# Revit family: JoistGirder_NewMillennium
name_source: partatom
category: Structural Framing
units: mm (PartAtom-declared; Revit-internal decimal feet)

## family parameters
Always export as geometry = No
Always vertical = Yes
Classification Number = 23.25.30.21.14.11
Cut with Voids When Loaded = No
Material for Model Behavior = Steel
Section Shape = Not Defined
Shared = No
Show family pre-cut in plan views = Yes

## types (116) — shared parameters
Angle Size_Lower = 0' - 6"
Angle Size_Upper = 0' - 6"
Assembly Code = B1010464
Bearing Seat = Yes
Bottom Chord Offset from End = 3' - 0"
Building Codes = https://www.newmill.com
Channel Width = 0' - 1 1/8"
Construction Details = https://www.newmill.com
Description = New Millennium Building Systems Joist Girder
Green Building-LEED = http://www.arcat.com
Installation-Fabrication = https://www.newmill.com
Keynote = 05 21 00
Manufacturer = New Millennium Building Systems
Manufacturer Fax = 260-868-6002
Manufacturer Website = https://www.newmill.com
Model = Joist Girder
Product Data = http://www.arcat.com
Revision = R0_10-2017
Roundover = 0' - 0 1/4"
Sales Information = https://www.newmill.com
Seat Length = 1' - 0"
SeatHalf = 0' - 6 9/16"
SeatWdth = 0' - 2 1/8"
Specification = http://www.arcat.com
Test Data = https://www.newmill.com
Thickness = 0' - 0 1/2"
Thickness_Channel = 0' - 0 3/16"
Type Comments = Contact New Millennium for Structural Web Design
URL = https://www.newmill.com

## per-type parameters (varying)
| type | Beam Depth |
| 120 Ft Length x 120 in Depth | 10' - 0" |
| 120 Ft Length x 114 in Depth | 9' - 6" |
| 120 Ft Length x 108 in Depth | 9' - 0" |
| 120 Ft Length x 102 in Depth | 8' - 6" |
| 120 Ft Length x 96 in Depth | 8' - 0" |
| 110 Ft Length x 120 in Depth | 10' - 0" |
| 110 Ft Length x 114 in Depth | 9' - 6" |
| 110 Ft Length x 108 in Depth | 9' - 0" |
| 110 Ft Length x 96 in Depth | 8' - 0" |
| 110 Ft Length x 84 in Depth | 7' - 0" |
| 100 Ft Length x 120 in Depth | 10' - 0" |
| 100 Ft Length x 108 in Depth | 9' - 0" |
| 100 Ft Length x 102 in Depth | 8' - 6" |
| 100 Ft Length x 96 in Depth | 8' - 0" |
| 100 Ft Length x 84 in Depth | 7' - 0" |
| 100 Ft Length x 78 in Depth | 6' - 6" |
| 90 Ft Length x 108 in Depth | 9' - 0" |
| 90 Ft Length x 102 in Depth | 8' - 6" |
| 90 Ft Length x 96 in Depth | 8' - 0" |
| 90 Ft Length x 90 in Depth | 7' - 6" |
| 90 Ft Length x 84 in Depth | 7' - 0" |
| 90 Ft Length x 72 in Depth | 6' - 0" |
| 80 Ft Length x 96 in Depth | 8' - 0" |
| 80 Ft Length x 90 in Depth | 7' - 6" |
| 80 Ft Length x 84 in Depth | 7' - 0" |
| 80 Ft Length x 78 in Depth | 6' - 6" |
| 80 Ft Length x 72 in Depth | 6' - 0" |
| 80 Ft Length x 66 in Depth | 5' - 6" |
| 80 Ft Length x 60 in Depth | 5' - 0" |
| 75 Ft Length x 90 in Depth | 7' - 6" |
| 75 Ft Length x 84 in Depth | 7' - 0" |
| 75 Ft Length x 78 in Depth | 6' - 6" |
| 75 Ft Length x 72 in Depth | 6' - 0" |
| 75 Ft Length x 66 in Depth | 5' - 6" |
| 75 Ft Length x 60 in Depth | 5' - 0" |
| 75 Ft Length x 56 in Depth | 4' - 8" |
| 70 Ft Length x 84 in Depth | 7' - 0" |
| 70 Ft Length x 78 in Depth | 6' - 6" |
| 70 Ft Length x 72 in Depth | 6' - 0" |
| 70 Ft Length x 66 in Depth | 5' - 6" |
| 70 Ft Length x 60 in Depth | 5' - 0" |
| 70 Ft Length x 56 in Depth | 4' - 8" |
| 65 Ft Length x 72 in Depth | 6' - 0" |
| 65 Ft Length x 66 in Depth | 5' - 6" |
| 65 Ft Length x 60 in Depth | 5' - 0" |
| 65 Ft Length x 56 in Depth | 4' - 8" |
| 65 Ft Length x 52 in Depth | 4' - 4" |
| 60 Ft Length x 72 in Depth | 6' - 0" |
| 60 Ft Length x 66 in Depth | 5' - 6" |
| 60 Ft Length x 60 in Depth | 5' - 0" |
| 60 Ft Length x 56 in Depth | 4' - 8" |
| 60 Ft Length x 52 in Depth | 4' - 4" |
| 60 Ft Length x 48 in Depth | 4' - 0" |
| 55 Ft Length x 66 in Depth | 5' - 6" |
| 55 Ft Length x 60 in Depth | 5' - 0" |
| 55 Ft Length x 56 in Depth | 4' - 8" |
| 55 Ft Length x 52 in Depth | 4' - 4" |
| 55 Ft Length x 48 in Depth | 4' - 0" |
| 55 Ft Length x 44 in Depth | 3' - 8" |
| 50 Ft Length x 60 in Depth | 5' - 0" |
| 50 Ft Length x 56 in Depth | 4' - 8" |
| 50 Ft Length x 52 in Depth | 4' - 4" |
| 50 Ft Length x 48 in Depth | 4' - 0" |
| 50 Ft Length x 44 in Depth | 3' - 8" |
| 50 Ft Length x 40 in Depth | 3' - 4" |
| 48 Ft Length x 56 in Depth | 4' - 8" |
| 48 Ft Length x 52 in Depth | 4' - 4" |
| 48 Ft Length x 48 in Depth | 4' - 0" |
| 48 Ft Length x 44 in Depth | 3' - 8" |
| 48 Ft Length x 40 in Depth | 3' - 4" |
| 48 Ft Length x 36 in Depth | 3' - 0" |
| 45 Ft Length x 52 in Depth | 4' - 4" |
| 45 Ft Length x 48 in Depth | 4' - 0" |
| 45 Ft Length x 44 in Depth | 3' - 8" |
| 45 Ft Length x 40 in Depth | 3' - 4" |
| 45 Ft Length x 36 in Depth | 3' - 0" |
| 42 Ft Length x 48 in Depth | 4' - 0" |
| 42 Ft Length x 44 in Depth | 3' - 8" |
| 42 Ft Length x 40 in Depth | 3' - 4" |
| 42 Ft Length x 36 in Depth | 3' - 0" |
| 42 Ft Length x 32 in Depth | 2' - 8" |
| 40 Ft Length x 48 in Depth | 4' - 0" |
| 40 Ft Length x 44 in Depth | 3' - 8" |
| 40 Ft Length x 40 in Depth | 3' - 4" |
| 40 Ft Length x 36 in Depth | 3' - 0" |
| 40 Ft Length x 32 in Depth | 2' - 8" |
| 38 Ft Length x 44 in Depth | 3' - 8" |
| 38 Ft Length x 40 in Depth | 3' - 4" |
| 38 Ft Length x 36 in Depth | 3' - 0" |
| 38 Ft Length x 32 in Depth | 2' - 8" |
| 35 Ft Length x 40 in Depth | 3' - 4" |
| 35 Ft Length x 36 in Depth | 3' - 0" |
| 35 Ft Length x 32 in Depth | 2' - 8" |
| 35 Ft Length x 28 in Depth | 2' - 4" |
| 32 Ft Length x 36 in Depth | 3' - 0" |
| 32 Ft Length x 32 in Depth | 2' - 8" |
| 32 Ft Length x 28 in Depth | 2' - 4" |
| 32 Ft Length x 24 in Depth | 2' - 0" |
| 30 Ft Length x 36 in Depth | 3' - 0" |
| 30 Ft Length x 32 in Depth | 2' - 8" |
| 30 Ft Length x 28 in Depth | 2' - 4" |
| 30 Ft Length x 24 in Depth | 2' - 0" |
| 28 Ft Length x 32 in Depth | 2' - 8" |
| 28 Ft Length x 28 in Depth | 2' - 4" |
| 28 Ft Length x 24 in Depth | 2' - 0" |
| 25 Ft Length x 36 in Depth | 3' - 0" |
| 25 Ft Length x 32 in Depth | 2' - 8" |
| 25 Ft Length x 28 in Depth | 2' - 4" |
| 25 Ft Length x 24 in Depth | 2' - 0" |
| 25 Ft Length x 20 in Depth | 1' - 8" |
| 22 Ft Length x 28 in Depth | 2' - 4" |
| 22 Ft Length x 24 in Depth | 2' - 0" |
| 22 Ft Length x 20 in Depth | 1' - 8" |
| 20 Ft Length x 28 in Depth | 2' - 4" |
| 20 Ft Length x 24 in Depth | 2' - 0" |
| 20 Ft Length x 20 in Depth | 1' - 8" |

## geometry (parser evidence)
native form markers: Sweep x4
no freeform markers — native parametric forms only
